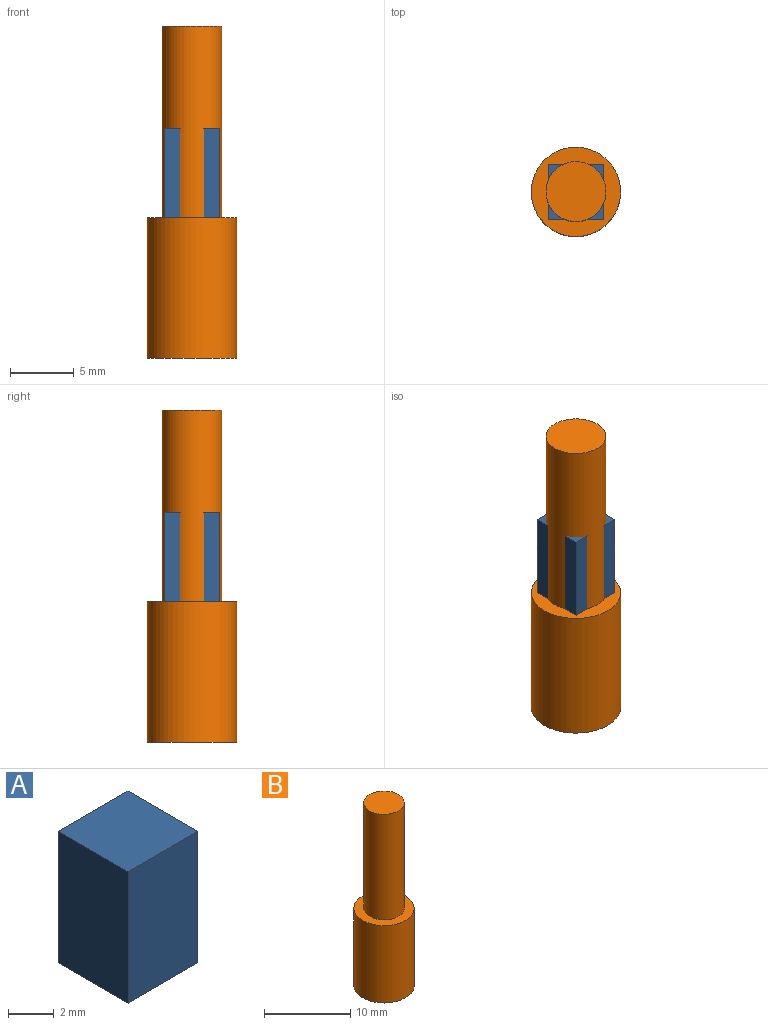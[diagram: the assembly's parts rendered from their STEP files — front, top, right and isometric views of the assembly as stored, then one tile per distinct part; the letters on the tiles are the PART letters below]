
ASSEMBLY  parts=2 mates=1
PART A: 6 faces, bbox 4.3x4.3x7 mm
  f0: plane 7x4.3mm, normal (0,-1,0), area 30.1mm2, adj f1,f3,f4,f5
  f1: plane 7x4.3mm, normal (1,0,0), area 30.1mm2, adj f0,f2,f4,f5
  f2: plane 7x4.3mm, normal (0,1,0), area 30.1mm2, adj f1,f3,f4,f5
  f3: plane 7x4.3mm, normal (-1,0,0), area 30.1mm2, adj f0,f2,f4,f5
  f4: plane 4.3x4.3mm, normal (0,0,1), area 18.5mm2, adj f0,f1,f2,f3
  f5: plane 4.3x4.3mm, normal (0,0,-1), area 18.5mm2, adj f0,f1,f2,f3
PART B: 5 faces, bbox 7x7x26 mm
  f0: cylinder r=3.5mm len=11mm, axis (0,0,-1), area 241.9mm2, adj f1,f2
  f1: plane 7x7mm, normal (0,0,1), area 21.1mm2, adj f0,f3
  f2: plane 7x7mm, normal (0,0,-1), area 38.5mm2, adj f0
  f3: cylinder r=2.35mm len=15mm, axis (0,0,-1), area 221.5mm2, adj f1,f4
  f4: plane 4.7x4.7mm, normal (0,0,1), area 17.3mm2, adj f3
PLACE A t=(-0.98,-5.67,-10.66)mm
PLACE B t=(-0.98,-5.67,-21.66)mm
MATE fastened A.f5 <-> B.f3  axis (0,0,-1) through (-0.98,-5.67,-10.66)mm
